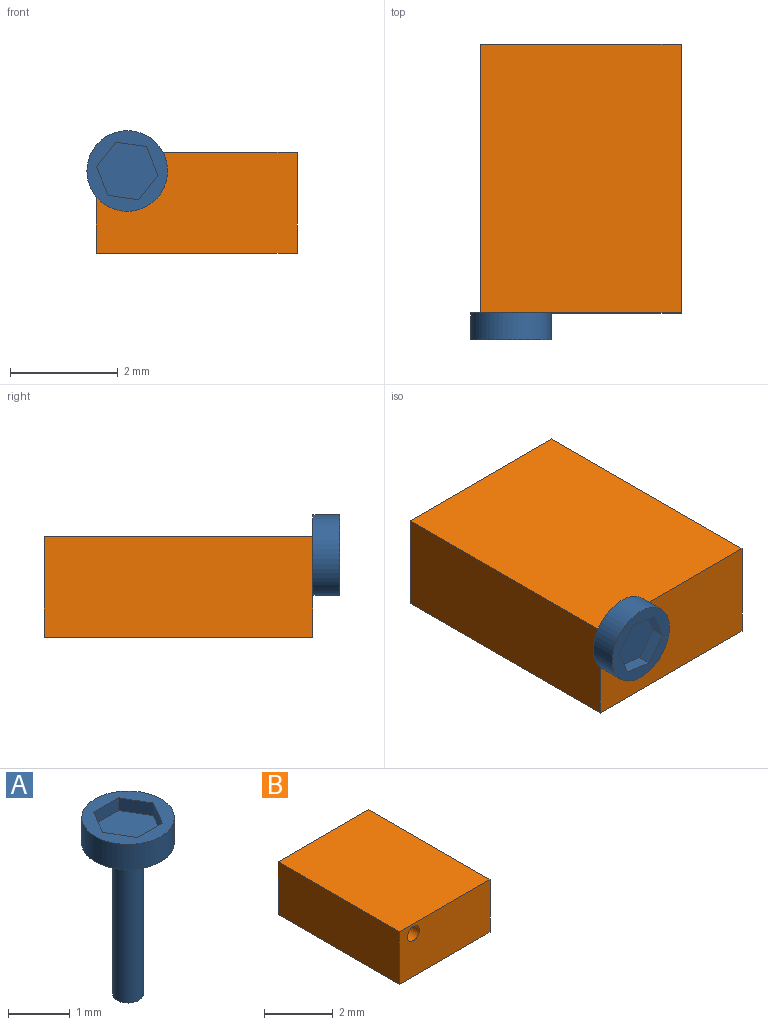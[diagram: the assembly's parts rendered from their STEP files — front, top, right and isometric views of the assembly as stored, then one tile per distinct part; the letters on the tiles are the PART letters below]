
ASSEMBLY  parts=2 mates=1
PART A: 12 faces, bbox 1.5x1.5x3.5 mm
  f0: plane 1.5x1.5mm, normal (0,0,1), area 0.9mm2, adj f4,f5,f6,f7,f8,f9,f10
  f1: plane 0.5x0.5mm, normal (0,0,-1), area 0.2mm2, adj f2
  f2: cylinder r=0.25mm len=3mm, axis (0,0,1), area 4.7mm2, adj f1,f3
  f3: plane 1.5x1.5mm, normal (0,0,-1), area 1.6mm2, adj f2,f4
  f4: cylinder r=0.75mm len=1.5mm, axis (0,0,1), area 2.4mm2, adj f0,f3
  f5: plane 0.5x0.29mm, normal (0.87,0.5,0), area 0.1mm2, adj f0,f6,f10,f11
  f6: plane 0.58x0.25mm, normal (0,1,0), area 0.1mm2, adj f0,f5,f7,f11
  f7: plane 0.5x0.29mm, normal (-0.87,0.5,0), area 0.1mm2, adj f0,f6,f8,f11
  f8: plane 0.5x0.29mm, normal (-0.87,-0.5,0), area 0.1mm2, adj f0,f7,f9,f11
  f9: plane 0.58x0.25mm, normal (0,-1,0), area 0.1mm2, adj f0,f8,f10,f11
  f10: plane 0.5x0.29mm, normal (0.87,-0.5,0), area 0.1mm2, adj f0,f5,f9,f11
  f11: plane 1.15x1mm, normal (0,0,1), area 0.9mm2, adj f5,f6,f7,f8,f9,f10
PART B: 7 faces, bbox 3.7x5x1.9 mm
  f0: plane 5x3.74mm, normal (0,0,1), area 18.7mm2, adj f1,f4,f5,f6
  f1: plane 5x1.88mm, normal (-1,0,0), area 9.4mm2, adj f0,f2,f5,f6
  f2: plane 5x3.74mm, normal (0,0,-1), area 18.7mm2, adj f1,f4,f5,f6
  f3: cylinder r=0.25mm len=5mm, axis (0,1,0), area 7.9mm2, adj f5,f6
  f4: plane 5x1.88mm, normal (1,0,0), area 9.4mm2, adj f0,f2,f5,f6
  f5: plane 3.74x1.88mm, normal (0,-1,0), area 6.8mm2, adj f0,f1,f2,f3,f4
  f6: plane 3.74x1.88mm, normal (0,1,0), area 6.8mm2, adj f0,f1,f2,f3,f4
PLACE A rot(axis=(0.05,-0.71,0.71),174.3deg) t=(-1.89,-2.93,1.21)mm
PLACE B t=(1.31,2.57,-20.89)mm fixed
MATE cylindrical B.f3 <-> A.f2  axis (0,1,0) through (-1.89,-2.43,1.21)mm
